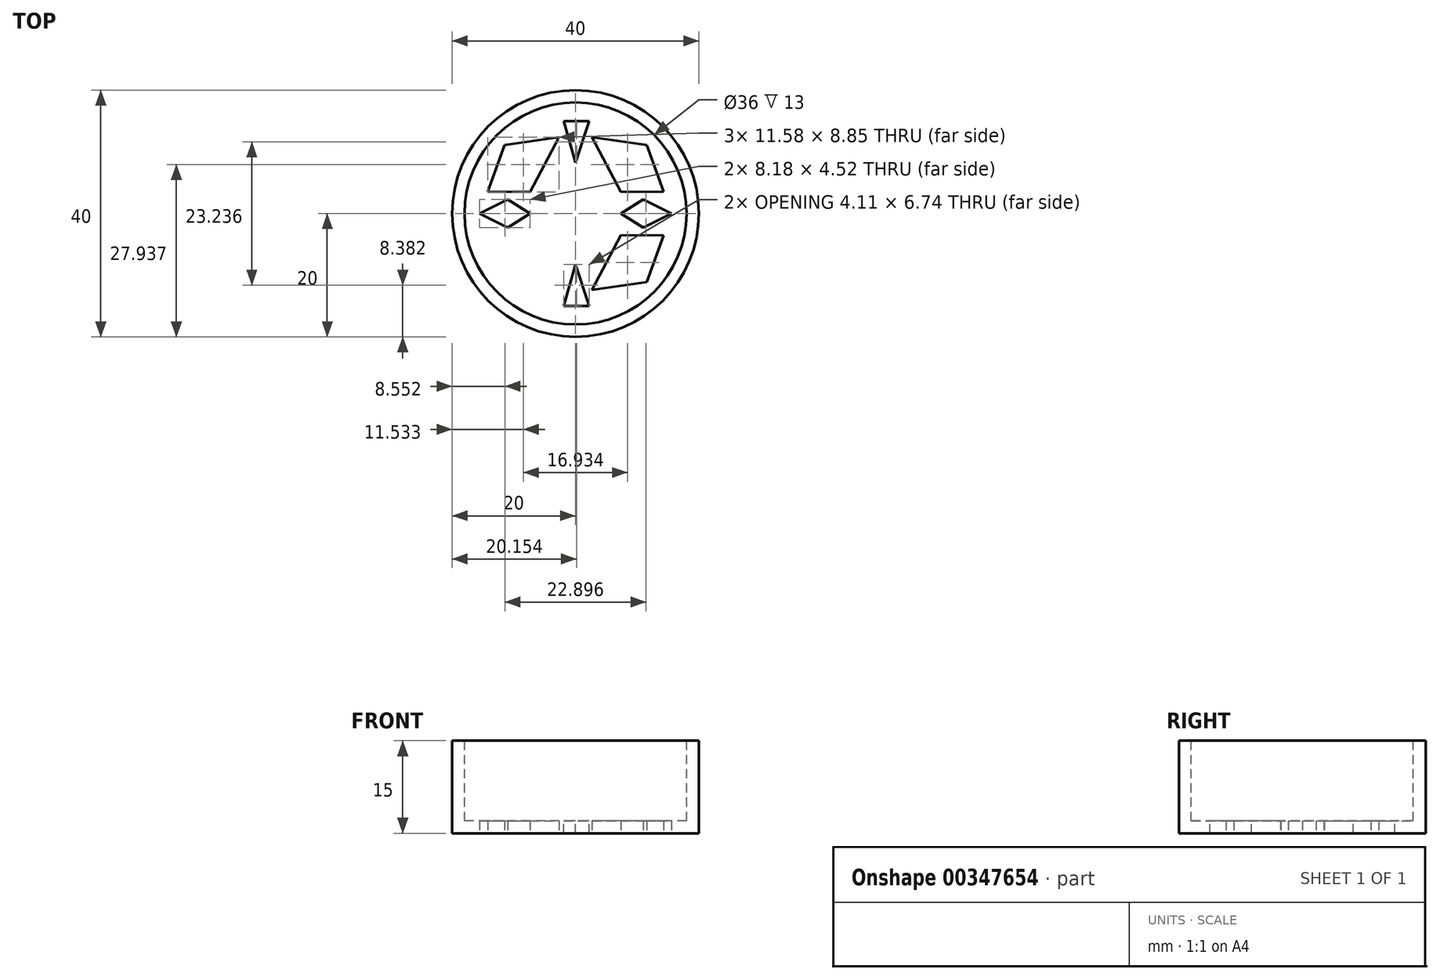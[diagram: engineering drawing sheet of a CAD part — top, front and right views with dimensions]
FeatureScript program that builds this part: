
annotation { "Feature Type Name" : "Feature", "Feature Type Description" : "" }
export const myFeature = defineFeature(function(context is Context, id is Id, definition is map)
    precondition{}
    {
        {
            var Q0;
            Q0=qCreatedBy(makeId("Top.planeOp"),FACE);
            var sketch = newSketch(context, id + "F0", { "sketchPlane" : qUnion([Q0])});
            skCircle(sketch, "E0", {"center": v(0, 0) * mm, "radius": 20 * mm});
            skSolve(sketch);
        }
        {
            var Q0;
            Q0=makeQuery(id+"F0.imprint","IMPRINT",FACE,{"disambiguationData":[TD([[makeQuery(id+"F0.imprint","IMPRINT",EDGE,{"derivedFrom":sQuery(id+"F0.wireOp",EDGE,"E0")}),1.0]])]});
            extrude(context, id + "F1", {"entities" : qUnion([Q0]), "depth" : 15 * mm});
        }
        {
            var Q0;
            Q0=makeQuery(id+"F1.opExtrude","CAP_FACE",FACE,{"disambiguationData":[OSD([sQuery(id+"F0.wireOp",EDGE,"E0")])],"isStart":false});
            var sketch = newSketch(context, id + "F2", { "sketchPlane" : qUnion([Q0])});
            skCircle(sketch, "E1", {"center": v(0, 0) * mm, "radius": 18 * mm});
            skSolve(sketch);
        }
        {
            var Q0;
            Q0=makeQuery(id+"F2.imprint","IMPRINT",FACE,{"disambiguationData":[TD([[makeQuery(id+"F2.imprint","IMPRINT",EDGE,{"derivedFrom":sQuery(id+"F2.wireOp",EDGE,"E1")}),1.0]])]});
            extrude(context, id + "F3", {"entities" : qUnion([Q0]), "operationType" : NewBodyOperationType.REMOVE, "oppositeDirection" : true, "depth" : 13 * mm});
        }
        {
            var Q0;
            Q0=makeQuery(id+"F3.boolean.opBoolean","COPY",FACE,{"derivedFrom":makeQuery(id+"F3.opExtrude","CAP_FACE",FACE,{"disambiguationData":[OSD([sQuery(id+"F2.wireOp",EDGE,"E1")])],"isStart":false})});
            var sketch = newSketch(context, id + "F4", { "sketchPlane" : qUnion([Q0])});
            skSolve(sketch);
        }
        {
            var Q0;
            Q0=makeQuery(id+"F4.imprint","IMPRINT",FACE,{"disambiguationData":[TD([[makeQuery(id+"F4.imprint","IMPRINT",EDGE,{"derivedFrom":makeQuery(id+"F3.boolean.opBoolean","COPY",EDGE,{"derivedFrom":makeQuery(id+"F3.opExtrude","CAP_EDGE",EDGE,{"disambiguationData":[OSD([sQuery(id+"F2.wireOp",EDGE,"E1")])],"isStart":false})})}),1.0]])]});
            var sketch = newSketch(context, id + "F5", { "sketchPlane" : qUnion([Q0])});
            skCircle(sketch, "E2", {"center": v(0, 0) * mm, "radius": 3.5 * mm});
            skCircle(sketch, "E3", {"center": v(0, 0) * mm, "radius": 1.5 * mm});
            skSolve(sketch);
        }
        {
            var Q0;
            Q0=qCreatedBy(makeId("Right.planeOp"),FACE);
            var sketch = newSketch(context, id + "F6", { "sketchPlane" : qUnion([Q0])});
            skSolve(sketch);
        }
        {
            var Q0;
            Q0=sQuery(id+"F5.wireOp",EDGE,"E2");
            var Q1;
            Q1 = qConstructionFilter(qBodyType(qCreatedBy(id + "F6" ,EDGE), BodyType.WIRE), ConstructionObject.NO);
            var Q2;
            Q2=sQuery(id+"F5.wireOp",EDGE,"E3");
            extrude(context, id + "F7", {"bodyType" : ToolBodyType.SURFACE, "surfaceEntities" : qUnion([Q0, Q1, Q2]), "depth" : 16 * mm});
        }
        {
            var Q0;
            Q0=makeQuery(id+"F1.opExtrude","CAP_FACE",FACE,{"disambiguationData":[OSD([sQuery(id+"F0.wireOp",EDGE,"E0")])],"isStart":true});
            var sketch = newSketch(context, id + "F8", { "sketchPlane" : qUnion([Q0])});
            skLineSegment(sketch, "E4", {"start": v(-14.26, 3.58) * mm, "end": v(-11.53, 11.13) * mm});
            skLineSegment(sketch, "E5", {"start": v(-11.53, 11.13) * mm, "end": v(-2.68, 12.36) * mm});
            skLineSegment(sketch, "E6.MirrorCS", {"start": v(14.26, 3.58) * mm, "end": v(11.53, 11.13) * mm});
            skLineSegment(sketch, "E7.MirrorCS", {"start": v(11.53, 11.13) * mm, "end": v(2.68, 12.36) * mm});
            skLineSegment(sketch, "E8.MirrorCS", {"start": v(14.26, -3.58) * mm, "end": v(11.53, -11.13) * mm});
            skLineSegment(sketch, "E9.MirrorCS", {"start": v(11.53, -11.13) * mm, "end": v(2.68, -12.36) * mm});
            skLineSegment(sketch, "E10.MirrorCS", {"start": v(-11.53, -11.13) * mm, "end": v(-2.68, -12.36) * mm});
            skLineSegment(sketch, "E11.MirrorCS", {"start": v(-14.26, -3.58) * mm, "end": v(-11.53, -11.13) * mm});
            skLineSegment(sketch, "E12", {"start": v(2.68, -12.36) * mm, "end": v(7.35, -3.51) * mm});
            skLineSegment(sketch, "E13", {"start": v(7.35, -3.51) * mm, "end": v(14.26, -3.58) * mm});
            skLineSegment(sketch, "E14.MirrorCS", {"start": v(7.35, 3.51) * mm, "end": v(14.26, 3.58) * mm});
            skLineSegment(sketch, "E15.MirrorCS", {"start": v(2.68, 12.36) * mm, "end": v(7.35, 3.51) * mm});
            skLineSegment(sketch, "E16.MirrorCS", {"start": v(-2.68, -12.36) * mm, "end": v(-7.35, -3.51) * mm});
            skLineSegment(sketch, "E17.MirrorCS", {"start": v(-7.35, -3.51) * mm, "end": v(-14.26, -3.58) * mm});
            skLineSegment(sketch, "E18.MirrorCS", {"start": v(-2.68, 12.36) * mm, "end": v(-7.35, 3.51) * mm});
            skLineSegment(sketch, "E19.MirrorCS", {"start": v(-7.35, 3.51) * mm, "end": v(-14.26, 3.58) * mm});
            skSolve(sketch);
        }
        {
            var Q0;
            Q0=makeQuery(id+"F8.imprint","IMPRINT",FACE,{"disambiguationData":[TD([[makeQuery(id+"F8.imprint","IMPRINT",EDGE,{"derivedFrom":sQuery(id+"F8.wireOp",EDGE,"E4")}),-1.0]])]});
            var Q1;
            Q1=makeQuery(id+"F8.imprint","IMPRINT",FACE,{"disambiguationData":[TD([[makeQuery(id+"F8.imprint","IMPRINT",EDGE,{"derivedFrom":sQuery(id+"F8.wireOp",EDGE,"E6.MirrorCS")}),1.0]])]});
            var Q2;
            Q2=makeQuery(id+"F8.imprint","IMPRINT",FACE,{"disambiguationData":[TD([[makeQuery(id+"F8.imprint","IMPRINT",EDGE,{"derivedFrom":sQuery(id+"F8.wireOp",EDGE,"E8.MirrorCS")}),-1.0]])]});
            var Q3;
            Q3=makeQuery(id+"F8.imprint","IMPRINT",FACE,{"disambiguationData":[TD([[makeQuery(id+"F8.imprint","IMPRINT",EDGE,{"derivedFrom":sQuery(id+"F8.wireOp",EDGE,"E11.MirrorCS")}),1.0]])]});
            extrude(context, id + "F9", {"entities" : qUnion([Q0, Q1, Q2, Q3]), "operationType" : NewBodyOperationType.REMOVE, "oppositeDirection" : true, "depth" : 8.7 * mm});
        }
        {
            var Q0;
            Q0=makeQuery(id+"F1.opExtrude","CAP_FACE",FACE,{"disambiguationData":[OSD([sQuery(id+"F0.wireOp",EDGE,"E0")])],"isStart":true});
            var sketch = newSketch(context, id + "F10", { "sketchPlane" : qUnion([Q0])});
            skLineSegment(sketch, "E20", {"start": v(13.86, 0.83) * mm, "end": v(10.97, 2.26) * mm});
            skLineSegment(sketch, "E21", {"start": v(10.97, 2.26) * mm, "end": v(5.61, -1.1) * mm});
            skLineSegment(sketch, "E22", {"start": v(5.61, -1.1) * mm, "end": v(10.97, 2.26) * mm});
            skLineSegment(sketch, "E23", {"start": v(13.86, 0.83) * mm, "end": v(17.9, -1.17) * mm});
            skLineSegment(sketch, "E24.MirrorCS", {"start": v(5.61, 1.1) * mm, "end": v(10.97, -2.26) * mm});
            skLineSegment(sketch, "E25.MirrorCS", {"start": v(13.86, -0.83) * mm, "end": v(10.97, -2.26) * mm});
            skLineSegment(sketch, "E26.MirrorCS", {"start": v(13.86, -0.83) * mm, "end": v(17.9, 1.17) * mm});
            skLineSegment(sketch, "E27.MirrorCS", {"start": v(-5.61, 1.1) * mm, "end": v(-10.97, -2.26) * mm});
            skLineSegment(sketch, "E28.MirrorCS", {"start": v(-5.61, -1.1) * mm, "end": v(-10.97, 2.26) * mm});
            skLineSegment(sketch, "E29.MirrorCS", {"start": v(-13.86, 0.83) * mm, "end": v(-10.97, 2.26) * mm});
            skLineSegment(sketch, "E30.MirrorCS", {"start": v(-13.86, 0.83) * mm, "end": v(-17.9, -1.17) * mm});
            skLineSegment(sketch, "E31.MirrorCS", {"start": v(-13.86, -0.83) * mm, "end": v(-17.9, 1.17) * mm});
            skLineSegment(sketch, "E32.MirrorCS", {"start": v(-13.86, -0.83) * mm, "end": v(-10.97, -2.26) * mm});
            skSolve(sketch);
        }
        {
            var Q0;
            {var subQ5=sQuery(id+"F10.wireOp",EDGE,"E20");Q0=makeQuery(id+"F10.imprint","IMPRINT",FACE,{"disambiguationData":[TD([[makeQuery(id+"F10.imprint","IMPRINT",EDGE,{"derivedFrom":subQ5}),1.0]])]});}
            var Q1;
            {var subQ1=sQuery(id+"F10.wireOp",EDGE,"E29.MirrorCS");Q1=makeQuery(id+"F10.imprint","IMPRINT",FACE,{"disambiguationData":[TD([[makeQuery(id+"F10.imprint","IMPRINT",EDGE,{"derivedFrom":subQ1}),-1.0]])]});}
            extrude(context, id + "F11", {"entities" : qUnion([Q0, Q1]), "operationType" : NewBodyOperationType.REMOVE, "oppositeDirection" : true, "depth" : 11 * mm});
        }
        {
            var Q0;
            Q0=makeQuery(id+"F4.imprint","IMPRINT",FACE,{"disambiguationData":[TD([[makeQuery(id+"F4.imprint","IMPRINT",EDGE,{"derivedFrom":makeQuery(id+"F3.boolean.opBoolean","COPY",EDGE,{"derivedFrom":makeQuery(id+"F3.opExtrude","CAP_EDGE",EDGE,{"disambiguationData":[OSD([sQuery(id+"F2.wireOp",EDGE,"E1")])],"isStart":false})})}),1.0]])]});
            var sketch = newSketch(context, id + "F12", { "sketchPlane" : qUnion([Q0])});
            skLineSegment(sketch, "E33", {"start": v(-1.9, 14.99) * mm, "end": v(2.2, 14.99) * mm});
            skLineSegment(sketch, "E34", {"start": v(2.2, 14.99) * mm, "end": v(0, 8.25) * mm});
            skLineSegment(sketch, "E35", {"start": v(0, 8.25) * mm, "end": v(-1.9, 14.99) * mm});
            skLineSegment(sketch, "E36.MirrorCS", {"start": v(2.2, -14.99) * mm, "end": v(0, -8.25) * mm});
            skLineSegment(sketch, "E37.MirrorCS", {"start": v(-1.9, -14.99) * mm, "end": v(2.2, -14.99) * mm});
            skLineSegment(sketch, "E38.MirrorCS", {"start": v(0, -8.25) * mm, "end": v(-1.9, -14.99) * mm});
            skSolve(sketch);
        }
        {
            var Q0;
            Q0=makeQuery(id+"F12.imprint","IMPRINT",FACE,{"disambiguationData":[TD([[makeQuery(id+"F12.imprint","IMPRINT",EDGE,{"derivedFrom":sQuery(id+"F12.wireOp",EDGE,"E33")}),-1.0]])]});
            var Q1;
            Q1=makeQuery(id+"F12.imprint","IMPRINT",FACE,{"disambiguationData":[TD([[makeQuery(id+"F12.imprint","IMPRINT",EDGE,{"derivedFrom":sQuery(id+"F12.wireOp",EDGE,"E36.MirrorCS")}),1.0]])]});
            extrude(context, id + "F13", {"entities" : qUnion([Q0, Q1]), "operationType" : NewBodyOperationType.REMOVE, "depth" : 22.4 * mm});
        }
        {
            var Q0;
            Q0 = qSketchRegion(id + "F12", true);
            extrude(context, id + "F14", {"entities" : qUnion([Q0]), "operationType" : NewBodyOperationType.REMOVE, "oppositeDirection" : true, "depth" : 4.9 * mm});
        }
    });
